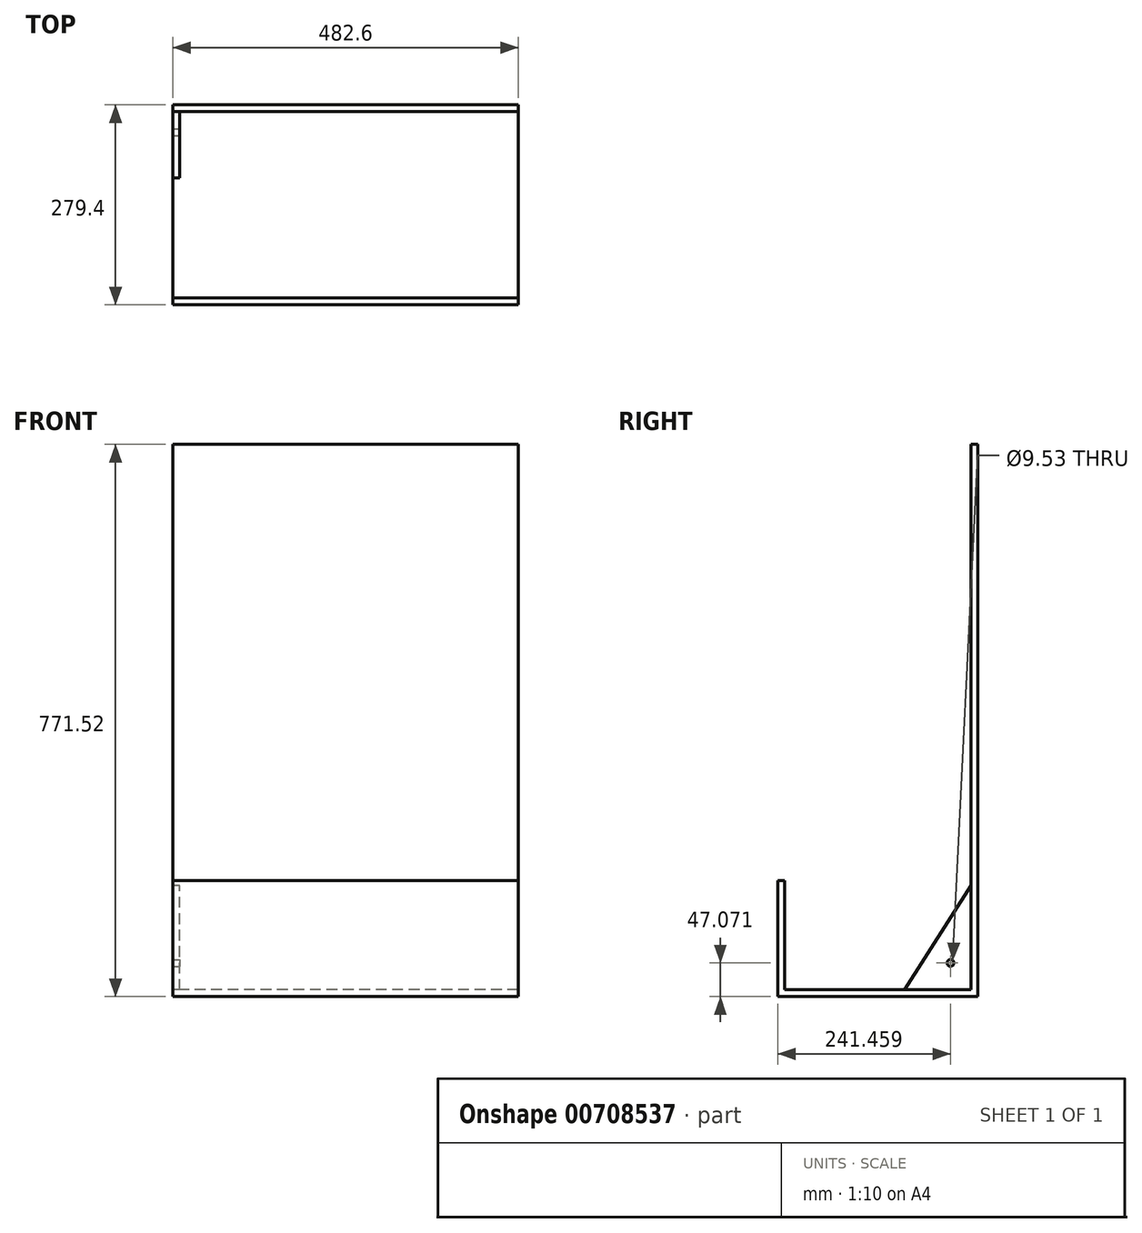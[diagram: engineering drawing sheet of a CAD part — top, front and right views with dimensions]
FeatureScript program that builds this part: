
annotation { "Feature Type Name" : "Feature", "Feature Type Description" : "" }
export const myFeature = defineFeature(function(context is Context, id is Id, definition is map)
    precondition{}
    {
        {
            var Q0;
            Q0=qCreatedBy(makeId("Top.planeOp"),FACE);
            var sketch = newSketch(context, id + "F0", { "sketchPlane" : qUnion([Q0])});
            skLineSegment(sketch, "E0.bottom", {"start": v(241.3, -139.7) * mm, "end": v(-241.3, -139.7) * mm});
            skLineSegment(sketch, "E0.top", {"start": v(241.3, 139.7) * mm, "end": v(-241.3, 139.7) * mm});
            skLineSegment(sketch, "E0.left", {"start": v(241.3, -139.7) * mm, "end": v(241.3, 139.7) * mm});
            skLineSegment(sketch, "E0.right", {"start": v(-241.3, -139.7) * mm, "end": v(-241.3, 139.7) * mm});
            skPoint(sketch, "E0.middle", {"position": v(0, 0) * mm});
            skSolve(sketch);
        }
        {
            var Q0;
            Q0=makeQuery(id+"F0.imprint","IMPRINT",FACE,{"disambiguationData":[TD([[makeQuery(id+"F0.imprint","IMPRINT",EDGE,{"derivedFrom":sQuery(id+"F0.wireOp",EDGE,"E0.bottom")}),-1.0]])]});
            extrude(context, id + "F1", {"entities" : qUnion([Q0]), "endBound" : BoundingType.SYMMETRIC, "depth" : 9.52 * mm, "offsetDistance" : 25.4 * mm});
        }
        {
            var Q0;
            Q0=makeQuery(id+"F1.opExtrude","SWEPT_FACE",FACE,{"disambiguationData":[OSD([sQuery(id+"F0.wireOp",EDGE,"E0.top")])]});
            var sketch = newSketch(context, id + "F2", { "sketchPlane" : qUnion([Q0])});
            skLineSegment(sketch, "E1.bottom", {"start": v(241.3, 4.76) * mm, "end": v(-241.3, 4.76) * mm});
            skLineSegment(sketch, "E1.top", {"start": v(241.3, 766.76) * mm, "end": v(-241.3, 766.76) * mm});
            skLineSegment(sketch, "E1.left", {"start": v(241.3, 4.76) * mm, "end": v(241.3, 766.76) * mm});
            skLineSegment(sketch, "E1.right", {"start": v(-241.3, 4.76) * mm, "end": v(-241.3, 766.76) * mm});
            skSolve(sketch);
        }
        {
            var Q0;
            Q0 = qSketchRegion(id + "F2", true);
            extrude(context, id + "F3", {"entities" : qUnion([Q0]), "operationType" : NewBodyOperationType.ADD, "oppositeDirection" : true, "depth" : 9.52 * mm, "offsetDistance" : 25.4 * mm});
        }
        {
            var Q0;
            Q0=makeQuery(id+"F1.opExtrude","SWEPT_FACE",FACE,{"disambiguationData":[OSD([sQuery(id+"F0.wireOp",EDGE,"E0.bottom")])]});
            var sketch = newSketch(context, id + "F4", { "sketchPlane" : qUnion([Q0])});
            skLineSegment(sketch, "E2.bottom", {"start": v(-241.3, 4.76) * mm, "end": v(241.3, 4.76) * mm});
            skLineSegment(sketch, "E2.top", {"start": v(-241.3, 157.16) * mm, "end": v(241.3, 157.16) * mm});
            skLineSegment(sketch, "E2.left", {"start": v(-241.3, 4.76) * mm, "end": v(-241.3, 157.16) * mm});
            skLineSegment(sketch, "E2.right", {"start": v(241.3, 4.76) * mm, "end": v(241.3, 157.16) * mm});
            skSolve(sketch);
        }
        {
            var Q0;
            Q0=makeQuery(id+"F4.imprint","IMPRINT",FACE,{"disambiguationData":[TD([[makeQuery(id+"F4.imprint","IMPRINT",EDGE,{"derivedFrom":sQuery(id+"F4.wireOp",EDGE,"E2.bottom")}),-1.0]])]});
            extrude(context, id + "F5", {"entities" : qUnion([Q0]), "operationType" : NewBodyOperationType.ADD, "oppositeDirection" : true, "depth" : 9.52 * mm, "offsetDistance" : 25.4 * mm});
        }
        {
            var Q0;
            Q0=makeQuery(id+"F5.boolean.opBoolean","MERGE",FACE,{"derivedFrom":[makeQuery(id+"F3.boolean.opBoolean","MERGE",FACE,{"derivedFrom":[makeQuery(id+"F1.opExtrude","SWEPT_FACE",FACE,{"disambiguationData":[OSD([sQuery(id+"F0.wireOp",EDGE,"E0.right")])]}),makeQuery(id+"F3.opExtrude","SWEPT_FACE",FACE,{"disambiguationData":[OSD([sQuery(id+"F2.wireOp",EDGE,"E1.left")])]})]}),makeQuery(id+"F5.opExtrude","SWEPT_FACE",FACE,{"disambiguationData":[OSD([sQuery(id+"F4.wireOp",EDGE,"E2.left")])]})]});
            var sketch = newSketch(context, id + "F6", { "sketchPlane" : qUnion([Q0])});
            skLineSegment(sketch, "E3", {"start": v(-130.18, 150.38) * mm, "end": v(-37.95, 4.76) * mm});
            skSolve(sketch);
        }
        {
            var Q0;
            {var subQ0=sQuery(id+"F6.wireOp",EDGE,"E3");Q0=makeQuery(id+"F6.imprint","IMPRINT",FACE,{"disambiguationData":[TD([[makeQuery(id+"F6.imprint","IMPRINT",EDGE,{"derivedFrom":subQ0}),-1.0]])]});}
            extrude(context, id + "F7", {"entities" : qUnion([Q0]), "operationType" : NewBodyOperationType.ADD, "oppositeDirection" : true, "depth" : 9.52 * mm, "offsetDistance" : 25.4 * mm});
        }
        {
            var Q0;
            Q0=makeQuery(id+"FiRx4EOBbb1pAzi_1.1.F7.boolean.opBoolean","MERGE",FACE,{"derivedFrom":[makeQuery(id+"F5.boolean.opBoolean","MERGE",FACE,{"derivedFrom":[makeQuery(id+"F3.boolean.opBoolean","MERGE",FACE,{"derivedFrom":[makeQuery(id+"F1.opExtrude","SWEPT_FACE",FACE,{"disambiguationData":[OSD([sQuery(id+"F0.wireOp",EDGE,"E0.left")])]}),makeQuery(id+"F3.opExtrude","SWEPT_FACE",FACE,{"disambiguationData":[OSD([sQuery(id+"F2.wireOp",EDGE,"E1.right")])]})]}),makeQuery(id+"F5.opExtrude","SWEPT_FACE",FACE,{"disambiguationData":[OSD([sQuery(id+"F4.wireOp",EDGE,"E2.right")])]})]}),makeQuery(id+"FiRx4EOBbb1pAzi_1.1.F7.opExtrude","CAP_FACE",FACE,{"disambiguationData":[OSD([sQuery(id+"F0.wireOp",EDGE,"E0.right"),sQuery(id+"F2.wireOp",EDGE,"E1.left"),sQuery(id+"F6.wireOp",EDGE,"E3")])],"isStart":true})]});
            var sketch = newSketch(context, id + "F8", { "sketchPlane" : qUnion([Q0])});
            skPoint(sketch, "E4", {"position": v(101.76, 42.31) * mm});
            skSolve(sketch);
        }
        {
            var Q0;
            Q0=sQuery(id+"F8.wireOp",VERTEX,"E4");
            var Q1;
            Q1=makeQuery(id+"F1.opExtrude","SWEPT_BODY",BODY,{"disambiguationData":[OSD([sQuery(id+"F0.wireOp",EDGE,"E0.bottom"),sQuery(id+"F0.wireOp",EDGE,"E0.top"),sQuery(id+"F0.wireOp",EDGE,"E0.left"),sQuery(id+"F0.wireOp",EDGE,"E0.right")])]});
            hole(context, id + "F9", {"style" : HoleStyle.SIMPLE, "endStyle" : HoleEndStyle.THROUGH, "holeDiameter" : 9.52 * mm, "majorDiameter" : 6.35 * mm, "isTappedThrough" : true, "tappedDepth" : 12.7 * mm, "tapClearance" : 3, "locations" : qUnion([Q0]), "scope" : qUnion([Q1])});
        }
    });
